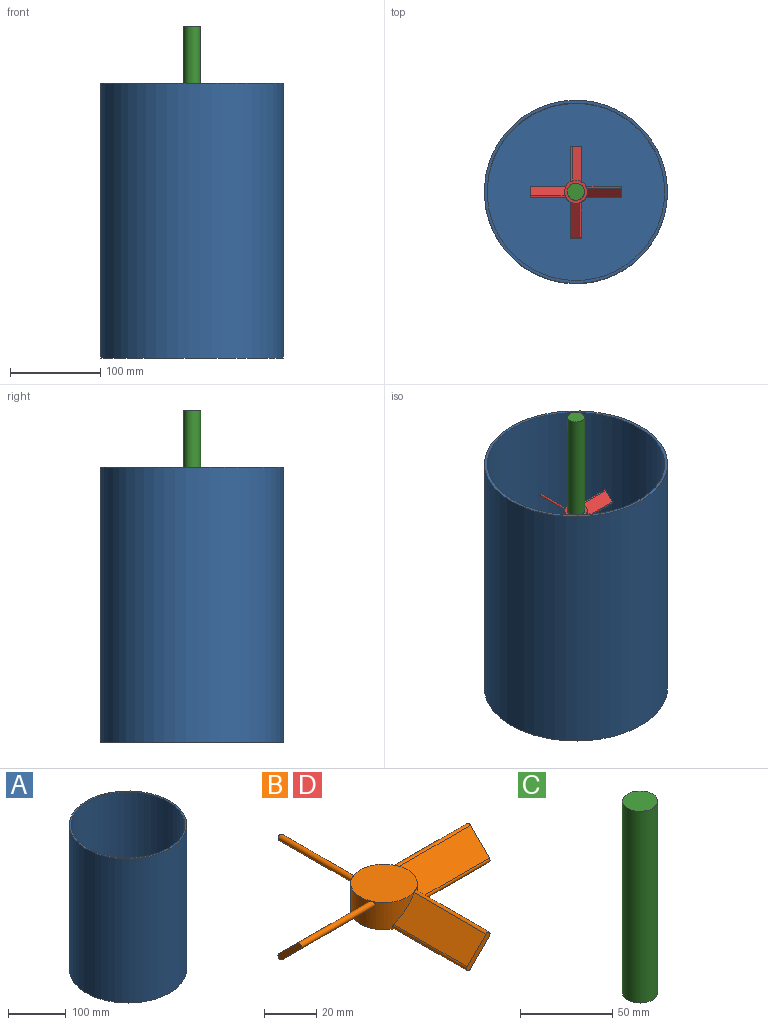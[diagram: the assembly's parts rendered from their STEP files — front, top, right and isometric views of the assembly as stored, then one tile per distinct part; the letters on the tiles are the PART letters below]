
ASSEMBLY  parts=4 mates=6
PART A: 5 faces, bbox 203.2x203.2x304.8 mm
  f0: cylinder r=101.6mm len=304.8mm, axis (0,0,-1), area 194575.7mm2, adj f1,f2
  f1: plane 203.2x203.2mm, normal (0,0,1), area 1995.2mm2, adj f0,f3
  f2: plane 203.2x203.2mm, normal (0,0,-1), area 32429.3mm2, adj f0
  f3: cylinder r=98.42mm len=301.63mm, axis (0,0,-1), area 186531.7mm2, adj f1,f4
  f4: plane 196.85x196.85mm, normal (0,0,1), area 30434.1mm2, adj f3
PART B: 26 faces, bbox 101.6x101.6x12.7 mm
  f0: cylinder r=12.7mm len=17.78mm, axis (0,0,-1), area 210.1mm2, adj f4,f5,f12,f14,f15,f17,f19,f20
  f1: cylinder r=12.7mm len=17.78mm, axis (0,0,-1), area 210.1mm2, adj f4,f5,f13,f14,f15,f21,f22,f24
  f2: cylinder r=12.7mm len=17.78mm, axis (0,0,-1), area 210.1mm2, adj f4,f5,f6,f7,f9,f21,f22,f23
  f3: cylinder r=12.7mm len=17.78mm, axis (0,0,-1), area 210.1mm2, adj f4,f5,f6,f7,f8,f18,f19,f20
  f4: plane 25.4x25.4mm, normal (0,0,1), area 506.7mm2, adj f0,f1,f2,f3
  f5: plane 25.4x25.4mm, normal (0,0,-1), area 506.7mm2, adj f0,f1,f2,f3
  f6: cylinder r=1.27mm len=39.8mm, axis (-1,0,0), area 157.4mm2, adj f2,f3,f8,f9,f10
  f7: cylinder r=1.27mm len=39.8mm, axis (-1,0,0), area 157.4mm2, adj f2,f3,f8,f9,f10
  f8: plane 39.6x10.16mm, normal (0,0.71,-0.71), area 552.9mm2, adj f3,f6,f7,f10
  f9: plane 39.6x10.16mm, normal (0,-0.71,0.71), area 552.9mm2, adj f2,f6,f7,f10
  f10: plane 12.7x12.7mm, normal (1,0,0), area 41.6mm2, adj f6,f7,f8,f9
  f11: plane 12.7x12.7mm, normal (-1,0,0), area 41.6mm2, adj f12,f13,f14,f15
  f12: plane 39.6x10.16mm, normal (0,0.71,0.71), area 552.9mm2, adj f0,f11,f14,f15
  f13: plane 39.6x10.16mm, normal (0,-0.71,-0.71), area 552.9mm2, adj f1,f11,f14,f15
  f14: cylinder r=1.27mm len=39.8mm, axis (1,0,0), area 157.4mm2, adj f0,f1,f11,f12,f13
  f15: cylinder r=1.27mm len=39.8mm, axis (1,0,0), area 157.4mm2, adj f0,f1,f11,f12,f13
  f16: plane 12.7x12.7mm, normal (0,1,0), area 41.6mm2, adj f17,f18,f19,f20
  f17: plane 39.6x10.16mm, normal (-0.71,0,-0.71), area 552.9mm2, adj f0,f16,f19,f20
  f18: plane 39.6x10.16mm, normal (0.71,0,0.71), area 552.9mm2, adj f3,f16,f19,f20
  f19: cylinder r=1.27mm len=39.8mm, axis (0,-1,0), area 157.4mm2, adj f0,f3,f16,f17,f18
  f20: cylinder r=1.27mm len=39.8mm, axis (0,-1,0), area 157.4mm2, adj f0,f3,f16,f17,f18
  f21: cylinder r=1.27mm len=39.8mm, axis (0,1,0), area 157.4mm2, adj f1,f2,f23,f24,f25
  f22: cylinder r=1.27mm len=39.8mm, axis (0,1,0), area 157.4mm2, adj f1,f2,f23,f24,f25
  f23: plane 39.6x10.16mm, normal (0.71,0,-0.71), area 552.9mm2, adj f2,f21,f22,f25
  f24: plane 39.6x10.16mm, normal (-0.71,0,0.71), area 552.9mm2, adj f1,f21,f22,f25
  f25: plane 12.7x12.7mm, normal (0,-1,0), area 41.6mm2, adj f21,f22,f23,f24
PART C: 3 faces, bbox 19.1x19.1x127 mm
  f0: cylinder r=9.53mm len=127mm, axis (0,0,-1), area 7600.6mm2, adj f1,f2
  f1: plane 19.05x19.05mm, normal (0,0,1), area 285mm2, adj f0
  f2: plane 19.05x19.05mm, normal (0,0,-1), area 285mm2, adj f0
PART D: same geometry as B
PLACE A at identity
PLACE B t=(0,0,9.52)mm
PLACE C rot(axis=(0,0,-1),35.9deg) t=(0,0,241.3)mm
PLACE D rot(axis=(0,0,1),180deg) t=(0,0,234.95)mm
MATE planar C.f0 <-> A.f0  axis (0,0,-1) through (0,0,304.8)mm
MATE revolute B.f0 <-> A.f0  axis (0,0,-1) through (0,0,3.17)mm
MATE revolute C.f0 <-> D.f0  axis (0,0,-1) through (0,0,241.3)mm
MATE planar D.f0 <-> C.f0  axis (0,0,1) through (0,0,241.3)mm
MATE planar B.f0 <-> A.f0  axis (0,0,-1) through (0,0,3.17)mm
MATE revolute C.f0 <-> A.f0  axis (0,0,-1) through (0,0,304.8)mm
